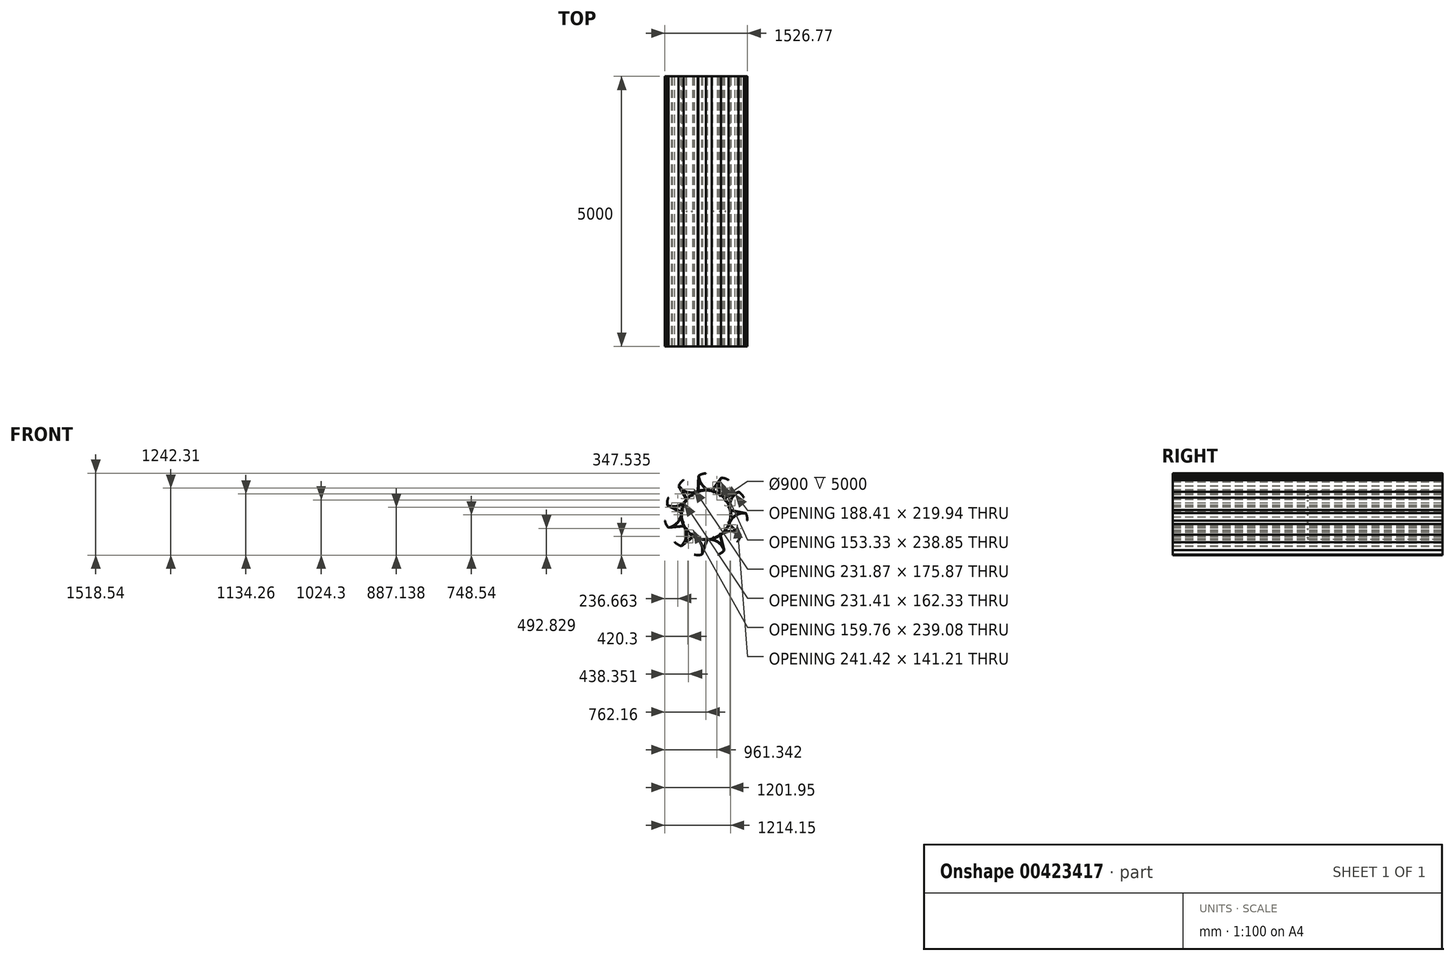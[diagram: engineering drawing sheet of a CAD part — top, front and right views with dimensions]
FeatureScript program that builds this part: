
annotation { "Feature Type Name" : "Feature", "Feature Type Description" : "" }
export const myFeature = defineFeature(function(context is Context, id is Id, definition is map)
    precondition{}
    {
        {
            var Q0;
            Q0=qCreatedBy(makeId("Front.planeOp"),FACE);
            var sketch = newSketch(context, id + "F0", { "sketchPlane" : qUnion([Q0])});
            skCircle(sketch, "E0", {"center": v(0, 0) * mm, "radius": 450 * mm});
            skCircle(sketch, "E1", {"center": v(0, 0) * mm, "radius": 465 * mm});
            skLineSegment(sketch, "E2", {"start": v(0, 765) * mm, "end": v(0, 465) * mm, "construction": true});
            skPoint(sketch, "E3", {"position": v(-130, 725) * mm});
            skLineSegment(sketch, "E4", {"start": v(0, 765) * mm, "end": v(0, 770) * mm});
            skArc(sketch, "E5", {"start": v(0, 765) * mm, "mid": v(-68, 754.77) * mm, "end": v(-130, 725) * mm});
            skArc(sketch, "E6", {"start": v(-130, 725) * mm, "mid": v(-60.31, 546.37) * mm, "end": v(106.9, 452.54) * mm});
            skArc(sketch, "E7", {"start": v(0, 770) * mm, "mid": v(-73.53, 758.47) * mm, "end": v(-140, 725) * mm});
            skPoint(sketch, "E8", {"position": v(0, 725) * mm});
            skLineSegment(sketch, "E9", {"start": v(-140, 725) * mm, "end": v(-154.73, 438.5) * mm});
            skLineSegment(sketch, "E10", {"start": v(-139.45, 443.6) * mm, "end": v(-129.04, 645.97) * mm});
            skArc(sketch, "E11", {"start": v(-129.04, 645.97) * mm, "mid": v(-68.94, 538.21) * mm, "end": v(29.67, 464.05) * mm});
            skArc(sketch, "E12.1.0", {"start": v(-501.33, 539.63) * mm, "mid": v(-346.13, 427.03) * mm, "end": v(-154.73, 438.5) * mm});
            skArc(sketch, "E12.1.1", {"start": v(-413.6, 643.56) * mm, "mid": v(-465.27, 598.19) * mm, "end": v(-501.33, 539.63) * mm});
            skLineSegment(sketch, "E12.1.2", {"start": v(-357.14, 297.79) * mm, "end": v(-457.8, 473.66) * mm});
            skPoint(sketch, "E12.1.3", {"position": v(-501.33, 539.63) * mm});
            skArc(sketch, "E12.1.4", {"start": v(-457.8, 473.66) * mm, "mid": v(-348.98, 415.5) * mm, "end": v(-225.92, 406.43) * mm});
            skLineSegment(sketch, "E12.1.5", {"start": v(-413.6, 643.56) * mm, "end": v(-251.4, 391.18) * mm, "construction": true});
            skLineSegment(sketch, "E12.1.6", {"start": v(-509.74, 534.22) * mm, "end": v(-367.24, 285.24) * mm});
            skArc(sketch, "E12.1.7", {"start": v(-416.3, 647.77) * mm, "mid": v(-471.92, 598.32) * mm, "end": v(-509.74, 534.22) * mm});
            skPoint(sketch, "E12.1.8", {"position": v(-391.96, 609.9) * mm});
            skLineSegment(sketch, "E12.1.9", {"start": v(-413.6, 643.56) * mm, "end": v(-416.3, 647.77) * mm});
            skArc(sketch, "E12.2.0", {"start": v(-713.49, 182.92) * mm, "mid": v(-522.05, 172.1) * mm, "end": v(-367.24, 285.24) * mm});
            skArc(sketch, "E12.2.1", {"start": v(-695.87, 317.8) * mm, "mid": v(-714.82, 251.68) * mm, "end": v(-713.49, 182.92) * mm});
            skLineSegment(sketch, "E12.2.2", {"start": v(-461.44, 57.43) * mm, "end": v(-641.2, 150.96) * mm});
            skPoint(sketch, "E12.2.3", {"position": v(-713.49, 182.92) * mm});
            skArc(sketch, "E12.2.4", {"start": v(-641.2, 150.96) * mm, "mid": v(-518.21, 160.87) * mm, "end": v(-409.8, 219.77) * mm});
            skLineSegment(sketch, "E12.2.5", {"start": v(-695.87, 317.8) * mm, "end": v(-422.98, 193.17) * mm, "construction": true});
            skLineSegment(sketch, "E12.2.6", {"start": v(-717.64, 173.83) * mm, "end": v(-463.15, 41.41) * mm});
            skArc(sketch, "E12.2.7", {"start": v(-700.42, 319.87) * mm, "mid": v(-720.48, 248.2) * mm, "end": v(-717.64, 173.83) * mm});
            skPoint(sketch, "E12.2.8", {"position": v(-659.48, 301.18) * mm});
            skLineSegment(sketch, "E12.2.9", {"start": v(-695.87, 317.8) * mm, "end": v(-700.42, 319.87) * mm});
            skArc(sketch, "E12.3.0", {"start": v(-699.12, -231.86) * mm, "mid": v(-532.23, -137.45) * mm, "end": v(-463.15, 41.41) * mm});
            skArc(sketch, "E12.3.1", {"start": v(-757.21, -108.87) * mm, "mid": v(-737.41, -174.73) * mm, "end": v(-699.12, -231.86) * mm});
            skLineSegment(sketch, "E12.3.2", {"start": v(-419.24, -201.16) * mm, "end": v(-621.03, -219.66) * mm});
            skPoint(sketch, "E12.3.3", {"position": v(-699.12, -231.86) * mm});
            skArc(sketch, "E12.3.4", {"start": v(-621.03, -219.66) * mm, "mid": v(-522.92, -144.83) * mm, "end": v(-463.55, -36.67) * mm});
            skLineSegment(sketch, "E12.3.5", {"start": v(-757.21, -108.87) * mm, "end": v(-460.27, -66.18) * mm, "construction": true});
            skLineSegment(sketch, "E12.3.6", {"start": v(-697.7, -241.75) * mm, "end": v(-412.02, -215.56) * mm});
            skArc(sketch, "E12.3.7", {"start": v(-762.16, -109.58) * mm, "mid": v(-740.29, -180.72) * mm, "end": v(-697.7, -241.75) * mm});
            skPoint(sketch, "E12.3.8", {"position": v(-717.62, -103.18) * mm});
            skLineSegment(sketch, "E12.3.9", {"start": v(-757.21, -108.87) * mm, "end": v(-762.16, -109.58) * mm});
            skArc(sketch, "E12.4.0", {"start": v(-462.79, -573.02) * mm, "mid": v(-373.42, -403.38) * mm, "end": v(-412.02, -215.56) * mm});
            skArc(sketch, "E12.4.1", {"start": v(-578.15, -500.97) * mm, "mid": v(-525.88, -545.67) * mm, "end": v(-462.79, -573.02) * mm});
            skLineSegment(sketch, "E12.4.2", {"start": v(-243.93, -395.88) * mm, "end": v(-403.69, -520.55) * mm});
            skPoint(sketch, "E12.4.3", {"position": v(-462.79, -573.02) * mm});
            skArc(sketch, "E12.4.4", {"start": v(-403.69, -520.55) * mm, "mid": v(-361.6, -404.56) * mm, "end": v(-370.14, -281.46) * mm});
            skLineSegment(sketch, "E12.4.5", {"start": v(-578.15, -500.97) * mm, "end": v(-351.42, -304.51) * mm, "construction": true});
            skLineSegment(sketch, "E12.4.6", {"start": v(-456.24, -580.58) * mm, "end": v(-230.07, -404.1) * mm});
            skArc(sketch, "E12.4.7", {"start": v(-581.93, -504.24) * mm, "mid": v(-525.07, -552.26) * mm, "end": v(-456.24, -580.58) * mm});
            skPoint(sketch, "E12.4.8", {"position": v(-547.92, -474.77) * mm});
            skLineSegment(sketch, "E12.4.9", {"start": v(-578.15, -500.97) * mm, "end": v(-581.93, -504.24) * mm});
            skArc(sketch, "E12.5.0", {"start": v(-79.52, -732.26) * mm, "mid": v(-96.06, -541.23) * mm, "end": v(-230.07, -404.1) * mm});
            skArc(sketch, "E12.5.1", {"start": v(-215.53, -734.01) * mm, "mid": v(-147.4, -743.36) * mm, "end": v(-79.52, -732.26) * mm});
            skLineSegment(sketch, "E12.5.2", {"start": v(8.82, -464.92) * mm, "end": v(-58.18, -656.16) * mm});
            skPoint(sketch, "E12.5.3", {"position": v(-79.52, -732.26) * mm});
            skArc(sketch, "E12.5.4", {"start": v(-58.18, -656.16) * mm, "mid": v(-85.48, -535.83) * mm, "end": v(-159.2, -436.9) * mm});
            skLineSegment(sketch, "E12.5.5", {"start": v(-215.53, -734.01) * mm, "end": v(-131, -446.16) * mm, "construction": true});
            skLineSegment(sketch, "E12.5.6", {"start": v(-69.93, -735.07) * mm, "end": v(24.92, -464.33) * mm});
            skArc(sketch, "E12.5.7", {"start": v(-216.93, -738.8) * mm, "mid": v(-143.14, -748.47) * mm, "end": v(-69.93, -735.07) * mm});
            skPoint(sketch, "E12.5.8", {"position": v(-204.26, -695.63) * mm});
            skLineSegment(sketch, "E12.5.9", {"start": v(-215.53, -734.01) * mm, "end": v(-216.93, -738.8) * mm});
            skArc(sketch, "E12.6.0", {"start": v(329, -659) * mm, "mid": v(211.8, -507.25) * mm, "end": v(24.92, -464.33) * mm});
            skArc(sketch, "E12.6.1", {"start": v(215.53, -734.01) * mm, "mid": v(277.9, -705.04) * mm, "end": v(329, -659) * mm});
            skLineSegment(sketch, "E12.6.2", {"start": v(258.78, -386.34) * mm, "end": v(305.8, -583.45) * mm});
            skPoint(sketch, "E12.6.3", {"position": v(329, -659) * mm});
            skArc(sketch, "E12.6.4", {"start": v(305.8, -583.45) * mm, "mid": v(217.78, -496.99) * mm, "end": v(102.27, -453.61) * mm});
            skLineSegment(sketch, "E12.6.5", {"start": v(215.53, -734.01) * mm, "end": v(131, -446.16) * mm, "construction": true});
            skLineSegment(sketch, "E12.6.6", {"start": v(338.59, -656.19) * mm, "end": v(272, -377.15) * mm});
            skArc(sketch, "E12.6.7", {"start": v(216.93, -738.8) * mm, "mid": v(284.24, -707.04) * mm, "end": v(338.59, -656.19) * mm});
            skPoint(sketch, "E12.6.8", {"position": v(204.26, -695.63) * mm});
            skLineSegment(sketch, "E12.6.9", {"start": v(215.53, -734.01) * mm, "end": v(216.93, -738.8) * mm});
            skArc(sketch, "E12.7.0", {"start": v(633.05, -376.53) * mm, "mid": v(452.42, -312.22) * mm, "end": v(272, -377.15) * mm});
            skArc(sketch, "E12.7.1", {"start": v(578.15, -500.97) * mm, "mid": v(614.96, -442.88) * mm, "end": v(633.05, -376.53) * mm});
            skLineSegment(sketch, "E12.7.2", {"start": v(426.57, -185.1) * mm, "end": v(572.7, -325.5) * mm});
            skPoint(sketch, "E12.7.3", {"position": v(633.05, -376.53) * mm});
            skArc(sketch, "E12.7.4", {"start": v(572.7, -325.5) * mm, "mid": v(451.9, -300.35) * mm, "end": v(331.28, -326.31) * mm});
            skLineSegment(sketch, "E12.7.5", {"start": v(578.15, -500.97) * mm, "end": v(351.42, -304.51) * mm, "construction": true});
            skLineSegment(sketch, "E12.7.6", {"start": v(639.6, -368.97) * mm, "end": v(432.72, -170.22) * mm});
            skArc(sketch, "E12.7.7", {"start": v(581.93, -504.24) * mm, "mid": v(621.37, -441.13) * mm, "end": v(639.6, -368.97) * mm});
            skPoint(sketch, "E12.7.8", {"position": v(547.92, -474.77) * mm});
            skLineSegment(sketch, "E12.7.9", {"start": v(578.15, -500.97) * mm, "end": v(581.93, -504.24) * mm});
            skArc(sketch, "E12.8.0", {"start": v(736.12, 25.5) * mm, "mid": v(549.4, -18.06) * mm, "end": v(432.72, -170.22) * mm});
            skArc(sketch, "E12.8.1", {"start": v(757.21, -108.87) * mm, "mid": v(756.77, -40.1) * mm, "end": v(736.12, 25.5) * mm});
            skLineSegment(sketch, "E12.8.2", {"start": v(458.93, 74.9) * mm, "end": v(657.76, 35.8) * mm});
            skPoint(sketch, "E12.8.3", {"position": v(736.12, 25.5) * mm});
            skArc(sketch, "E12.8.4", {"start": v(657.76, 35.8) * mm, "mid": v(542.55, -8.36) * mm, "end": v(455.1, -95.41) * mm});
            skLineSegment(sketch, "E12.8.5", {"start": v(757.21, -108.87) * mm, "end": v(460.27, -66.18) * mm, "construction": true});
            skLineSegment(sketch, "E12.8.6", {"start": v(737.54, 35.4) * mm, "end": v(456.06, 90.75) * mm});
            skArc(sketch, "E12.8.7", {"start": v(762.16, -109.58) * mm, "mid": v(761.22, -35.16) * mm, "end": v(737.54, 35.4) * mm});
            skPoint(sketch, "E12.8.8", {"position": v(717.62, -103.18) * mm});
            skLineSegment(sketch, "E12.8.9", {"start": v(757.21, -108.87) * mm, "end": v(762.16, -109.58) * mm});
            skArc(sketch, "E12.9.0", {"start": v(605.48, 419.43) * mm, "mid": v(471.94, 281.83) * mm, "end": v(456.06, 90.75) * mm});
            skArc(sketch, "E12.9.1", {"start": v(695.87, 317.8) * mm, "mid": v(658.32, 375.4) * mm, "end": v(605.48, 419.43) * mm});
            skLineSegment(sketch, "E12.9.2", {"start": v(345.58, 311.12) * mm, "end": v(533.99, 385.73) * mm});
            skPoint(sketch, "E12.9.3", {"position": v(605.48, 419.43) * mm});
            skArc(sketch, "E12.9.4", {"start": v(533.99, 385.73) * mm, "mid": v(460.94, 286.3) * mm, "end": v(434.44, 165.78) * mm});
            skLineSegment(sketch, "E12.9.5", {"start": v(695.87, 317.8) * mm, "end": v(422.98, 193.17) * mm, "construction": true});
            skLineSegment(sketch, "E12.9.6", {"start": v(601.33, 428.52) * mm, "end": v(334.6, 322.9) * mm});
            skArc(sketch, "E12.9.7", {"start": v(700.42, 319.87) * mm, "mid": v(659.39, 381.96) * mm, "end": v(601.33, 428.52) * mm});
            skPoint(sketch, "E12.9.8", {"position": v(659.48, 301.18) * mm});
            skLineSegment(sketch, "E12.9.9", {"start": v(695.87, 317.8) * mm, "end": v(700.42, 319.87) * mm});
            skArc(sketch, "E12.10.0", {"start": v(282.6, 680.2) * mm, "mid": v(244.65, 492.24) * mm, "end": v(334.6, 322.9) * mm});
            skArc(sketch, "E12.10.1", {"start": v(413.6, 643.56) * mm, "mid": v(350.85, 671.72) * mm, "end": v(282.6, 680.2) * mm});
            skLineSegment(sketch, "E12.10.2", {"start": v(122.52, 448.57) * mm, "end": v(240.68, 613.2) * mm});
            skPoint(sketch, "E12.10.3", {"position": v(282.6, 680.2) * mm});
            skArc(sketch, "E12.10.4", {"start": v(240.68, 613.2) * mm, "mid": v(232.98, 490.05) * mm, "end": v(275.85, 374.34) * mm});
            skLineSegment(sketch, "E12.10.5", {"start": v(413.6, 643.56) * mm, "end": v(251.4, 391.18) * mm, "construction": true});
            skLineSegment(sketch, "E12.10.6", {"start": v(274.19, 685.6) * mm, "end": v(106.9, 452.54) * mm});
            skArc(sketch, "E12.10.7", {"start": v(416.3, 647.77) * mm, "mid": v(348.2, 677.82) * mm, "end": v(274.19, 685.6) * mm});
            skPoint(sketch, "E12.10.8", {"position": v(391.96, 609.9) * mm});
            skLineSegment(sketch, "E12.10.9", {"start": v(413.6, 643.56) * mm, "end": v(416.3, 647.77) * mm});
            skSolve(sketch);
        }
        {
            var Q0;
            {var subQ1=sQuery(id+"F0.wireOp",EDGE,"27a553c3-0f80-4c9b-9862-33f1c9b085be.2.0");Q0=makeQuery(id+"F0.imprint","IMPRINT",FACE,{"disambiguationData":[TD([[makeQuery(id+"F0.imprint","IMPRINT",EDGE,{"derivedFrom":subQ1}),1.0]])]});}
            var Q1;
            {var subQ1=sQuery(id+"F0.wireOp",EDGE,"27a553c3-0f80-4c9b-9862-33f1c9b085be.1.0");Q1=makeQuery(id+"F0.imprint","IMPRINT",FACE,{"disambiguationData":[TD([[makeQuery(id+"F0.imprint","IMPRINT",EDGE,{"derivedFrom":subQ1}),1.0]])]});}
            var Q2;
            Q2=makeQuery(id+"F0.imprint","IMPRINT",FACE,{"disambiguationData":[TD([[makeQuery(id+"F0.imprint","IMPRINT",EDGE,{"derivedFrom":sQuery(id+"F0.wireOp",EDGE,"E4")}),1.0]])]});
            var Q3;
            {var subQ1=sQuery(id+"F0.wireOp",EDGE,"27a553c3-0f80-4c9b-9862-33f1c9b085be.10.0");Q3=makeQuery(id+"F0.imprint","IMPRINT",FACE,{"disambiguationData":[TD([[makeQuery(id+"F0.imprint","IMPRINT",EDGE,{"derivedFrom":subQ1}),1.0]])]});}
            var Q4;
            {var subQ0=sQuery(id+"F0.wireOp",EDGE,"27a553c3-0f80-4c9b-9862-33f1c9b085be.9.0");Q4=makeQuery(id+"F0.imprint","IMPRINT",FACE,{"disambiguationData":[TD([[makeQuery(id+"F0.imprint","IMPRINT",EDGE,{"derivedFrom":subQ0}),1.0]])]});}
            var Q5;
            {var subQ1=sQuery(id+"F0.wireOp",EDGE,"27a553c3-0f80-4c9b-9862-33f1c9b085be.8.0");Q5=makeQuery(id+"F0.imprint","IMPRINT",FACE,{"disambiguationData":[TD([[makeQuery(id+"F0.imprint","IMPRINT",EDGE,{"derivedFrom":subQ1}),1.0]])]});}
            var Q6;
            {var subQ1=sQuery(id+"F0.wireOp",EDGE,"27a553c3-0f80-4c9b-9862-33f1c9b085be.7.0");Q6=makeQuery(id+"F0.imprint","IMPRINT",FACE,{"disambiguationData":[TD([[makeQuery(id+"F0.imprint","IMPRINT",EDGE,{"derivedFrom":subQ1}),1.0]])]});}
            var Q7;
            {var subQ0=sQuery(id+"F0.wireOp",EDGE,"27a553c3-0f80-4c9b-9862-33f1c9b085be.3.0");Q7=makeQuery(id+"F0.imprint","IMPRINT",FACE,{"disambiguationData":[TD([[makeQuery(id+"F0.imprint","IMPRINT",EDGE,{"derivedFrom":subQ0}),1.0]])]});}
            var Q8;
            {var subQ1=sQuery(id+"F0.wireOp",EDGE,"27a553c3-0f80-4c9b-9862-33f1c9b085be.4.0");Q8=makeQuery(id+"F0.imprint","IMPRINT",FACE,{"disambiguationData":[TD([[makeQuery(id+"F0.imprint","IMPRINT",EDGE,{"derivedFrom":subQ1}),1.0]])]});}
            var Q9;
            {var subQ0=sQuery(id+"F0.wireOp",EDGE,"27a553c3-0f80-4c9b-9862-33f1c9b085be.5.0");Q9=makeQuery(id+"F0.imprint","IMPRINT",FACE,{"disambiguationData":[TD([[makeQuery(id+"F0.imprint","IMPRINT",EDGE,{"derivedFrom":subQ0}),1.0]])]});}
            var Q10;
            {var subQ1=sQuery(id+"F0.wireOp",EDGE,"27a553c3-0f80-4c9b-9862-33f1c9b085be.6.0");Q10=makeQuery(id+"F0.imprint","IMPRINT",FACE,{"disambiguationData":[TD([[makeQuery(id+"F0.imprint","IMPRINT",EDGE,{"derivedFrom":subQ1}),1.0]])]});}
            var Q11;
            Q11=makeQuery(id+"F0.imprint","IMPRINT",FACE,{"disambiguationData":[TD([[makeQuery(id+"F0.imprint","IMPRINT",EDGE,{"derivedFrom":sQuery(id+"F0.wireOp",EDGE,"E0")}),-1.0]])]});
            var Q12;
            {var subQ0=sQuery(id+"F0.wireOp",EDGE,"E12.8.1");Q12=makeQuery(id+"F0.imprint","IMPRINT",FACE,{"disambiguationData":[TD([[makeQuery(id+"F0.imprint","IMPRINT",EDGE,{"derivedFrom":subQ0}),-1.0]])]});}
            var Q13;
            {var subQ0=sQuery(id+"F0.wireOp",EDGE,"E12.9.1");Q13=makeQuery(id+"F0.imprint","IMPRINT",FACE,{"disambiguationData":[TD([[makeQuery(id+"F0.imprint","IMPRINT",EDGE,{"derivedFrom":subQ0}),-1.0]])]});}
            var Q14;
            {var subQ0=sQuery(id+"F0.wireOp",EDGE,"E12.7.1");Q14=makeQuery(id+"F0.imprint","IMPRINT",FACE,{"disambiguationData":[TD([[makeQuery(id+"F0.imprint","IMPRINT",EDGE,{"derivedFrom":subQ0}),-1.0]])]});}
            var Q15;
            {var subQ0=sQuery(id+"F0.wireOp",EDGE,"E12.6.1");Q15=makeQuery(id+"F0.imprint","IMPRINT",FACE,{"disambiguationData":[TD([[makeQuery(id+"F0.imprint","IMPRINT",EDGE,{"derivedFrom":subQ0}),-1.0]])]});}
            var Q16;
            {var subQ0=sQuery(id+"F0.wireOp",EDGE,"E12.5.1");Q16=makeQuery(id+"F0.imprint","IMPRINT",FACE,{"disambiguationData":[TD([[makeQuery(id+"F0.imprint","IMPRINT",EDGE,{"derivedFrom":subQ0}),-1.0]])]});}
            var Q17;
            {var subQ0=sQuery(id+"F0.wireOp",EDGE,"E12.4.1");Q17=makeQuery(id+"F0.imprint","IMPRINT",FACE,{"disambiguationData":[TD([[makeQuery(id+"F0.imprint","IMPRINT",EDGE,{"derivedFrom":subQ0}),-1.0]])]});}
            var Q18;
            {var subQ0=sQuery(id+"F0.wireOp",EDGE,"E12.3.1");Q18=makeQuery(id+"F0.imprint","IMPRINT",FACE,{"disambiguationData":[TD([[makeQuery(id+"F0.imprint","IMPRINT",EDGE,{"derivedFrom":subQ0}),-1.0]])]});}
            var Q19;
            {var subQ0=sQuery(id+"F0.wireOp",EDGE,"E12.2.1");Q19=makeQuery(id+"F0.imprint","IMPRINT",FACE,{"disambiguationData":[TD([[makeQuery(id+"F0.imprint","IMPRINT",EDGE,{"derivedFrom":subQ0}),-1.0]])]});}
            var Q20;
            {var subQ0=sQuery(id+"F0.wireOp",EDGE,"E12.1.1");Q20=makeQuery(id+"F0.imprint","IMPRINT",FACE,{"disambiguationData":[TD([[makeQuery(id+"F0.imprint","IMPRINT",EDGE,{"derivedFrom":subQ0}),-1.0]])]});}
            var Q21;
            {var subQ0=sQuery(id+"F0.wireOp",EDGE,"E12.10.1");Q21=makeQuery(id+"F0.imprint","IMPRINT",FACE,{"disambiguationData":[TD([[makeQuery(id+"F0.imprint","IMPRINT",EDGE,{"derivedFrom":subQ0}),-1.0]])]});}
            extrude(context, id + "F1", {"entities" : qUnion([Q0, Q1, Q2, Q3, Q4, Q5, Q6, Q7, Q8, Q9, Q10, Q11, Q12, Q13, Q14, Q15, Q16, Q17, Q18, Q19, Q20, Q21]), "depth" : 5000 * mm});
        }
        {
            var Q0;
            Q0=qCreatedBy(makeId("Front.planeOp"),FACE);
            cPlane(context, id + "F2", {"entities" : qUnion([Q0]), "cplaneType" : CPlaneType.OFFSET, "offset" : 2500 * mm, "width" : 150 * mm, "height" : 150 * mm});
        }
        {
            var Q0;
            Q0=qCreatedBy(id+"F2.planeOp",FACE);
            var sketch = newSketch(context, id + "F3", { "sketchPlane" : qUnion([Q0])});
            skCircle(sketch, "E13", {"center": v(0, 0) * mm, "radius": 435 * mm, "construction": true});
            skCircle(sketch, "E14", {"center": v(0, 0) * mm, "radius": 450 * mm, "construction": true});
            skLineSegment(sketch, "E15", {"start": v(0, 0) * mm, "end": v(0, 450) * mm, "construction": true});
            skPoint(sketch, "E16", {"position": v(-7, 449.95) * mm});
            skPoint(sketch, "E17", {"position": v(7, 449.95) * mm});
            skArc(sketch, "E18", {"start": v(-7, 449.95) * mm, "mid": v(-5.98, 442.2) * mm, "end": v(-3, 434.99) * mm});
            skArc(sketch, "E19", {"start": v(3, 434.99) * mm, "mid": v(5.98, 442.2) * mm, "end": v(7, 449.95) * mm});
            skArc(sketch, "E20", {"start": v(-3, 434.99) * mm, "mid": v(0, 434.7) * mm, "end": v(3, 434.99) * mm});
            skArc(sketch, "E21", {"start": v(-7, 449.95) * mm, "mid": v(0, 450) * mm, "end": v(7, 449.95) * mm});
            skArc(sketch, "E22.1.0", {"start": v(-131.57, 414.63) * mm, "mid": v(-130.96, 422.41) * mm, "end": v(-132.38, 430.09) * mm});
            skPoint(sketch, "E22.1.1", {"position": v(-132.38, 430.09) * mm});
            skArc(sketch, "E22.1.2", {"start": v(-137.27, 412.77) * mm, "mid": v(-134.33, 413.42) * mm, "end": v(-131.57, 414.63) * mm});
            skArc(sketch, "E22.1.3", {"start": v(-145.7, 425.76) * mm, "mid": v(-139.06, 427.98) * mm, "end": v(-132.38, 430.09) * mm});
            skArc(sketch, "E22.1.4", {"start": v(-145.7, 425.76) * mm, "mid": v(-142.34, 418.71) * mm, "end": v(-137.27, 412.77) * mm});
            skPoint(sketch, "E22.1.5", {"position": v(-145.7, 425.76) * mm});
            skArc(sketch, "E22.2.0", {"start": v(-253.25, 353.68) * mm, "mid": v(-255.08, 361.27) * mm, "end": v(-258.8, 368.13) * mm});
            skPoint(sketch, "E22.2.1", {"position": v(-258.8, 368.13) * mm});
            skArc(sketch, "E22.2.2", {"start": v(-258.1, 350.15) * mm, "mid": v(-255.5, 351.67) * mm, "end": v(-253.25, 353.68) * mm});
            skArc(sketch, "E22.2.3", {"start": v(-270.13, 359.9) * mm, "mid": v(-264.5, 364.06) * mm, "end": v(-258.8, 368.13) * mm});
            skArc(sketch, "E22.2.4", {"start": v(-270.13, 359.9) * mm, "mid": v(-264.76, 354.23) * mm, "end": v(-258.1, 350.15) * mm});
            skPoint(sketch, "E22.2.5", {"position": v(-270.13, 359.9) * mm});
            skArc(sketch, "E22.3.0", {"start": v(-350.15, 258.1) * mm, "mid": v(-354.23, 264.76) * mm, "end": v(-359.9, 270.13) * mm});
            skPoint(sketch, "E22.3.1", {"position": v(-359.9, 270.13) * mm});
            skArc(sketch, "E22.3.2", {"start": v(-353.68, 253.25) * mm, "mid": v(-351.67, 255.5) * mm, "end": v(-350.15, 258.1) * mm});
            skArc(sketch, "E22.3.3", {"start": v(-368.13, 258.8) * mm, "mid": v(-364.06, 264.5) * mm, "end": v(-359.9, 270.13) * mm});
            skArc(sketch, "E22.3.4", {"start": v(-368.13, 258.8) * mm, "mid": v(-361.27, 255.08) * mm, "end": v(-353.68, 253.25) * mm});
            skPoint(sketch, "E22.3.5", {"position": v(-368.13, 258.8) * mm});
            skArc(sketch, "E22.4.0", {"start": v(-412.77, 137.27) * mm, "mid": v(-418.71, 142.34) * mm, "end": v(-425.76, 145.7) * mm});
            skPoint(sketch, "E22.4.1", {"position": v(-425.76, 145.7) * mm});
            skArc(sketch, "E22.4.2", {"start": v(-414.63, 131.57) * mm, "mid": v(-413.42, 134.33) * mm, "end": v(-412.77, 137.27) * mm});
            skArc(sketch, "E22.4.3", {"start": v(-430.09, 132.38) * mm, "mid": v(-427.98, 139.06) * mm, "end": v(-425.76, 145.7) * mm});
            skArc(sketch, "E22.4.4", {"start": v(-430.09, 132.38) * mm, "mid": v(-422.41, 130.96) * mm, "end": v(-414.63, 131.57) * mm});
            skPoint(sketch, "E22.4.5", {"position": v(-430.09, 132.38) * mm});
            skArc(sketch, "E22.5.0", {"start": v(-434.99, 3) * mm, "mid": v(-442.2, 5.98) * mm, "end": v(-449.95, 7) * mm});
            skPoint(sketch, "E22.5.1", {"position": v(-449.95, 7) * mm});
            skArc(sketch, "E22.5.2", {"start": v(-434.99, -3) * mm, "mid": v(-434.7, 0) * mm, "end": v(-434.99, 3) * mm});
            skArc(sketch, "E22.5.3", {"start": v(-449.95, -7) * mm, "mid": v(-450, 0) * mm, "end": v(-449.95, 7) * mm});
            skArc(sketch, "E22.5.4", {"start": v(-449.95, -7) * mm, "mid": v(-442.2, -5.98) * mm, "end": v(-434.99, -3) * mm});
            skPoint(sketch, "E22.5.5", {"position": v(-449.95, -7) * mm});
            skArc(sketch, "E22.6.0", {"start": v(-414.63, -131.57) * mm, "mid": v(-422.41, -130.96) * mm, "end": v(-430.09, -132.38) * mm});
            skPoint(sketch, "E22.6.1", {"position": v(-430.09, -132.38) * mm});
            skArc(sketch, "E22.6.2", {"start": v(-412.77, -137.27) * mm, "mid": v(-413.42, -134.33) * mm, "end": v(-414.63, -131.57) * mm});
            skArc(sketch, "E22.6.3", {"start": v(-425.76, -145.7) * mm, "mid": v(-427.98, -139.06) * mm, "end": v(-430.09, -132.38) * mm});
            skArc(sketch, "E22.6.4", {"start": v(-425.76, -145.7) * mm, "mid": v(-418.71, -142.34) * mm, "end": v(-412.77, -137.27) * mm});
            skPoint(sketch, "E22.6.5", {"position": v(-425.76, -145.7) * mm});
            skArc(sketch, "E22.7.0", {"start": v(-353.68, -253.25) * mm, "mid": v(-361.27, -255.08) * mm, "end": v(-368.13, -258.8) * mm});
            skPoint(sketch, "E22.7.1", {"position": v(-368.13, -258.8) * mm});
            skArc(sketch, "E22.7.2", {"start": v(-350.15, -258.1) * mm, "mid": v(-351.67, -255.5) * mm, "end": v(-353.68, -253.25) * mm});
            skArc(sketch, "E22.7.3", {"start": v(-359.9, -270.13) * mm, "mid": v(-364.06, -264.5) * mm, "end": v(-368.13, -258.8) * mm});
            skArc(sketch, "E22.7.4", {"start": v(-359.9, -270.13) * mm, "mid": v(-354.23, -264.76) * mm, "end": v(-350.15, -258.1) * mm});
            skPoint(sketch, "E22.7.5", {"position": v(-359.9, -270.13) * mm});
            skArc(sketch, "E22.8.0", {"start": v(-258.1, -350.15) * mm, "mid": v(-264.76, -354.23) * mm, "end": v(-270.13, -359.9) * mm});
            skPoint(sketch, "E22.8.1", {"position": v(-270.13, -359.9) * mm});
            skArc(sketch, "E22.8.2", {"start": v(-253.25, -353.68) * mm, "mid": v(-255.5, -351.67) * mm, "end": v(-258.1, -350.15) * mm});
            skArc(sketch, "E22.8.3", {"start": v(-258.8, -368.13) * mm, "mid": v(-264.5, -364.06) * mm, "end": v(-270.13, -359.9) * mm});
            skArc(sketch, "E22.8.4", {"start": v(-258.8, -368.13) * mm, "mid": v(-255.08, -361.27) * mm, "end": v(-253.25, -353.68) * mm});
            skPoint(sketch, "E22.8.5", {"position": v(-258.8, -368.13) * mm});
            skArc(sketch, "E22.9.0", {"start": v(-137.27, -412.77) * mm, "mid": v(-142.34, -418.71) * mm, "end": v(-145.7, -425.76) * mm});
            skPoint(sketch, "E22.9.1", {"position": v(-145.7, -425.76) * mm});
            skArc(sketch, "E22.9.2", {"start": v(-131.57, -414.63) * mm, "mid": v(-134.33, -413.42) * mm, "end": v(-137.27, -412.77) * mm});
            skArc(sketch, "E22.9.3", {"start": v(-132.38, -430.09) * mm, "mid": v(-139.06, -427.98) * mm, "end": v(-145.7, -425.76) * mm});
            skArc(sketch, "E22.9.4", {"start": v(-132.38, -430.09) * mm, "mid": v(-130.96, -422.41) * mm, "end": v(-131.57, -414.63) * mm});
            skPoint(sketch, "E22.9.5", {"position": v(-132.38, -430.09) * mm});
            skArc(sketch, "E22.10.0", {"start": v(-3, -434.99) * mm, "mid": v(-5.98, -442.2) * mm, "end": v(-7, -449.95) * mm});
            skPoint(sketch, "E22.10.1", {"position": v(-7, -449.95) * mm});
            skArc(sketch, "E22.10.2", {"start": v(3, -434.99) * mm, "mid": v(0, -434.7) * mm, "end": v(-3, -434.99) * mm});
            skArc(sketch, "E22.10.3", {"start": v(7, -449.95) * mm, "mid": v(0, -450) * mm, "end": v(-7, -449.95) * mm});
            skArc(sketch, "E22.10.4", {"start": v(7, -449.95) * mm, "mid": v(5.98, -442.2) * mm, "end": v(3, -434.99) * mm});
            skPoint(sketch, "E22.10.5", {"position": v(7, -449.95) * mm});
            skArc(sketch, "E22.11.0", {"start": v(131.57, -414.63) * mm, "mid": v(130.96, -422.41) * mm, "end": v(132.38, -430.09) * mm});
            skPoint(sketch, "E22.11.1", {"position": v(132.38, -430.09) * mm});
            skArc(sketch, "E22.11.2", {"start": v(137.27, -412.77) * mm, "mid": v(134.33, -413.42) * mm, "end": v(131.57, -414.63) * mm});
            skArc(sketch, "E22.11.3", {"start": v(145.7, -425.76) * mm, "mid": v(139.06, -427.98) * mm, "end": v(132.38, -430.09) * mm});
            skArc(sketch, "E22.11.4", {"start": v(145.7, -425.76) * mm, "mid": v(142.34, -418.71) * mm, "end": v(137.27, -412.77) * mm});
            skPoint(sketch, "E22.11.5", {"position": v(145.7, -425.76) * mm});
            skArc(sketch, "E22.12.0", {"start": v(253.25, -353.68) * mm, "mid": v(255.08, -361.27) * mm, "end": v(258.8, -368.13) * mm});
            skPoint(sketch, "E22.12.1", {"position": v(258.8, -368.13) * mm});
            skArc(sketch, "E22.12.2", {"start": v(258.1, -350.15) * mm, "mid": v(255.5, -351.67) * mm, "end": v(253.25, -353.68) * mm});
            skArc(sketch, "E22.12.3", {"start": v(270.13, -359.9) * mm, "mid": v(264.5, -364.06) * mm, "end": v(258.8, -368.13) * mm});
            skArc(sketch, "E22.12.4", {"start": v(270.13, -359.9) * mm, "mid": v(264.76, -354.23) * mm, "end": v(258.1, -350.15) * mm});
            skPoint(sketch, "E22.12.5", {"position": v(270.13, -359.9) * mm});
            skArc(sketch, "E22.13.0", {"start": v(350.15, -258.1) * mm, "mid": v(354.23, -264.76) * mm, "end": v(359.9, -270.13) * mm});
            skPoint(sketch, "E22.13.1", {"position": v(359.9, -270.13) * mm});
            skArc(sketch, "E22.13.2", {"start": v(353.68, -253.25) * mm, "mid": v(351.67, -255.5) * mm, "end": v(350.15, -258.1) * mm});
            skArc(sketch, "E22.13.3", {"start": v(368.13, -258.8) * mm, "mid": v(364.06, -264.5) * mm, "end": v(359.9, -270.13) * mm});
            skArc(sketch, "E22.13.4", {"start": v(368.13, -258.8) * mm, "mid": v(361.27, -255.08) * mm, "end": v(353.68, -253.25) * mm});
            skPoint(sketch, "E22.13.5", {"position": v(368.13, -258.8) * mm});
            skArc(sketch, "E22.14.0", {"start": v(412.77, -137.27) * mm, "mid": v(418.71, -142.34) * mm, "end": v(425.76, -145.7) * mm});
            skPoint(sketch, "E22.14.1", {"position": v(425.76, -145.7) * mm});
            skArc(sketch, "E22.14.2", {"start": v(414.63, -131.57) * mm, "mid": v(413.42, -134.33) * mm, "end": v(412.77, -137.27) * mm});
            skArc(sketch, "E22.14.3", {"start": v(430.09, -132.38) * mm, "mid": v(427.98, -139.06) * mm, "end": v(425.76, -145.7) * mm});
            skArc(sketch, "E22.14.4", {"start": v(430.09, -132.38) * mm, "mid": v(422.41, -130.96) * mm, "end": v(414.63, -131.57) * mm});
            skPoint(sketch, "E22.14.5", {"position": v(430.09, -132.38) * mm});
            skArc(sketch, "E22.15.0", {"start": v(434.99, -3) * mm, "mid": v(442.2, -5.98) * mm, "end": v(449.95, -7) * mm});
            skPoint(sketch, "E22.15.1", {"position": v(449.95, -7) * mm});
            skArc(sketch, "E22.15.2", {"start": v(434.99, 3) * mm, "mid": v(434.7, 0) * mm, "end": v(434.99, -3) * mm});
            skArc(sketch, "E22.15.3", {"start": v(449.95, 7) * mm, "mid": v(450, 0) * mm, "end": v(449.95, -7) * mm});
            skArc(sketch, "E22.15.4", {"start": v(449.95, 7) * mm, "mid": v(442.2, 5.98) * mm, "end": v(434.99, 3) * mm});
            skPoint(sketch, "E22.15.5", {"position": v(449.95, 7) * mm});
            skArc(sketch, "E22.16.0", {"start": v(414.63, 131.57) * mm, "mid": v(422.41, 130.96) * mm, "end": v(430.09, 132.38) * mm});
            skPoint(sketch, "E22.16.1", {"position": v(430.09, 132.38) * mm});
            skArc(sketch, "E22.16.2", {"start": v(412.77, 137.27) * mm, "mid": v(413.42, 134.33) * mm, "end": v(414.63, 131.57) * mm});
            skArc(sketch, "E22.16.3", {"start": v(425.76, 145.7) * mm, "mid": v(427.98, 139.06) * mm, "end": v(430.09, 132.38) * mm});
            skArc(sketch, "E22.16.4", {"start": v(425.76, 145.7) * mm, "mid": v(418.71, 142.34) * mm, "end": v(412.77, 137.27) * mm});
            skPoint(sketch, "E22.16.5", {"position": v(425.76, 145.7) * mm});
            skArc(sketch, "E22.17.0", {"start": v(353.68, 253.25) * mm, "mid": v(361.27, 255.08) * mm, "end": v(368.13, 258.8) * mm});
            skPoint(sketch, "E22.17.1", {"position": v(368.13, 258.8) * mm});
            skArc(sketch, "E22.17.2", {"start": v(350.15, 258.1) * mm, "mid": v(351.67, 255.5) * mm, "end": v(353.68, 253.25) * mm});
            skArc(sketch, "E22.17.3", {"start": v(359.9, 270.13) * mm, "mid": v(364.06, 264.5) * mm, "end": v(368.13, 258.8) * mm});
            skArc(sketch, "E22.17.4", {"start": v(359.9, 270.13) * mm, "mid": v(354.23, 264.76) * mm, "end": v(350.15, 258.1) * mm});
            skPoint(sketch, "E22.17.5", {"position": v(359.9, 270.13) * mm});
            skArc(sketch, "E22.18.0", {"start": v(258.1, 350.15) * mm, "mid": v(264.76, 354.23) * mm, "end": v(270.13, 359.9) * mm});
            skPoint(sketch, "E22.18.1", {"position": v(270.13, 359.9) * mm});
            skArc(sketch, "E22.18.2", {"start": v(253.25, 353.68) * mm, "mid": v(255.5, 351.67) * mm, "end": v(258.1, 350.15) * mm});
            skArc(sketch, "E22.18.3", {"start": v(258.8, 368.13) * mm, "mid": v(264.5, 364.06) * mm, "end": v(270.13, 359.9) * mm});
            skArc(sketch, "E22.18.4", {"start": v(258.8, 368.13) * mm, "mid": v(255.08, 361.27) * mm, "end": v(253.25, 353.68) * mm});
            skPoint(sketch, "E22.18.5", {"position": v(258.8, 368.13) * mm});
            skArc(sketch, "E22.19.0", {"start": v(137.27, 412.77) * mm, "mid": v(142.34, 418.71) * mm, "end": v(145.7, 425.76) * mm});
            skPoint(sketch, "E22.19.1", {"position": v(145.7, 425.76) * mm});
            skArc(sketch, "E22.19.2", {"start": v(131.57, 414.63) * mm, "mid": v(134.33, 413.42) * mm, "end": v(137.27, 412.77) * mm});
            skArc(sketch, "E22.19.3", {"start": v(132.38, 430.09) * mm, "mid": v(139.06, 427.98) * mm, "end": v(145.7, 425.76) * mm});
            skArc(sketch, "E22.19.4", {"start": v(132.38, 430.09) * mm, "mid": v(130.96, 422.41) * mm, "end": v(131.57, 414.63) * mm});
            skPoint(sketch, "E22.19.5", {"position": v(132.38, 430.09) * mm});
            skSolve(sketch);
        }
        {
            var Q0;
            Q0 = qSketchRegion(id + "F3", true);
            extrude(context, id + "F4", {"entities" : qUnion([Q0]), "operationType" : NewBodyOperationType.ADD, "depth" : 7 * mm, "hasSecondDirection" : true, "secondDirectionOppositeDirection" : true, "secondDirectionDepth" : 7 * mm});
        }
    });
